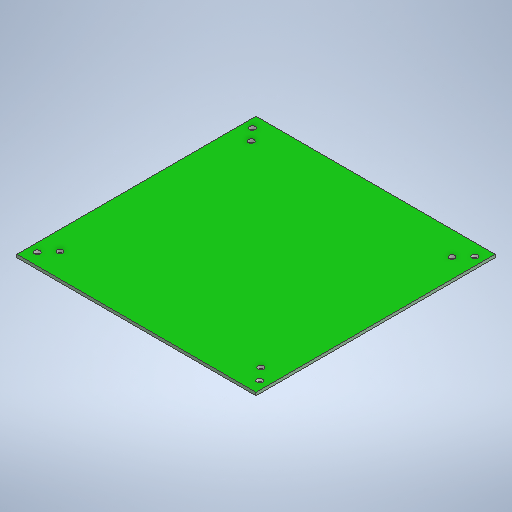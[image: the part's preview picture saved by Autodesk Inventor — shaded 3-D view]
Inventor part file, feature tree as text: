
AUTODESK INVENTOR PART (.ipt)
format: ipt  version: 2025.2 (Build 292293000, 293)  size: 252,928 bytes
history: native  units: in
note: dims shown in document units (in); Inventor stores cm internally (conversion verified against a paired STEP export)
features: extrude x3, sketch x3
ambient origin geometry x8: Origin, YZ Plane, XZ Plane, XY Plane, X Axis, Y Axis, Z Axis, Center Point
bodies: Solid1 (feature_tree)
feature tree (6):
  extrude  "Extrusion1"  Depth=5.0in
  extrude  "Extrusion2"  Depth=2.5in
  extrude  "Extrusion3"  Depth=0.0625in
  sketch  "Sketch1"  dims[d0=5.0in d1=5.0in]
  sketch  "Sketch2"  dims[d2=2.5in d3=2.5in]
  sketch  "Sketch3"  dims[d4=0.0625in d5=0.0in d6=0.12in d7=0.12in d8=0.12in d9=0.12in d10=4.5in d11=4.5in d12=0.0in d13=0.0in d14=0.0in d15=4.65in d16=0.25in d17=0.175in d18=0.0625in d19=0.0in d20=0.12in d21=0.12in d22=0.12in d23=0.12in d24=4.2in d25=4.2in d26=0.0in d27=4.0in d28=4.0in d29=0.0in d30=0.5in d31=0.4in d32=0.0625in d33=0.0in]
